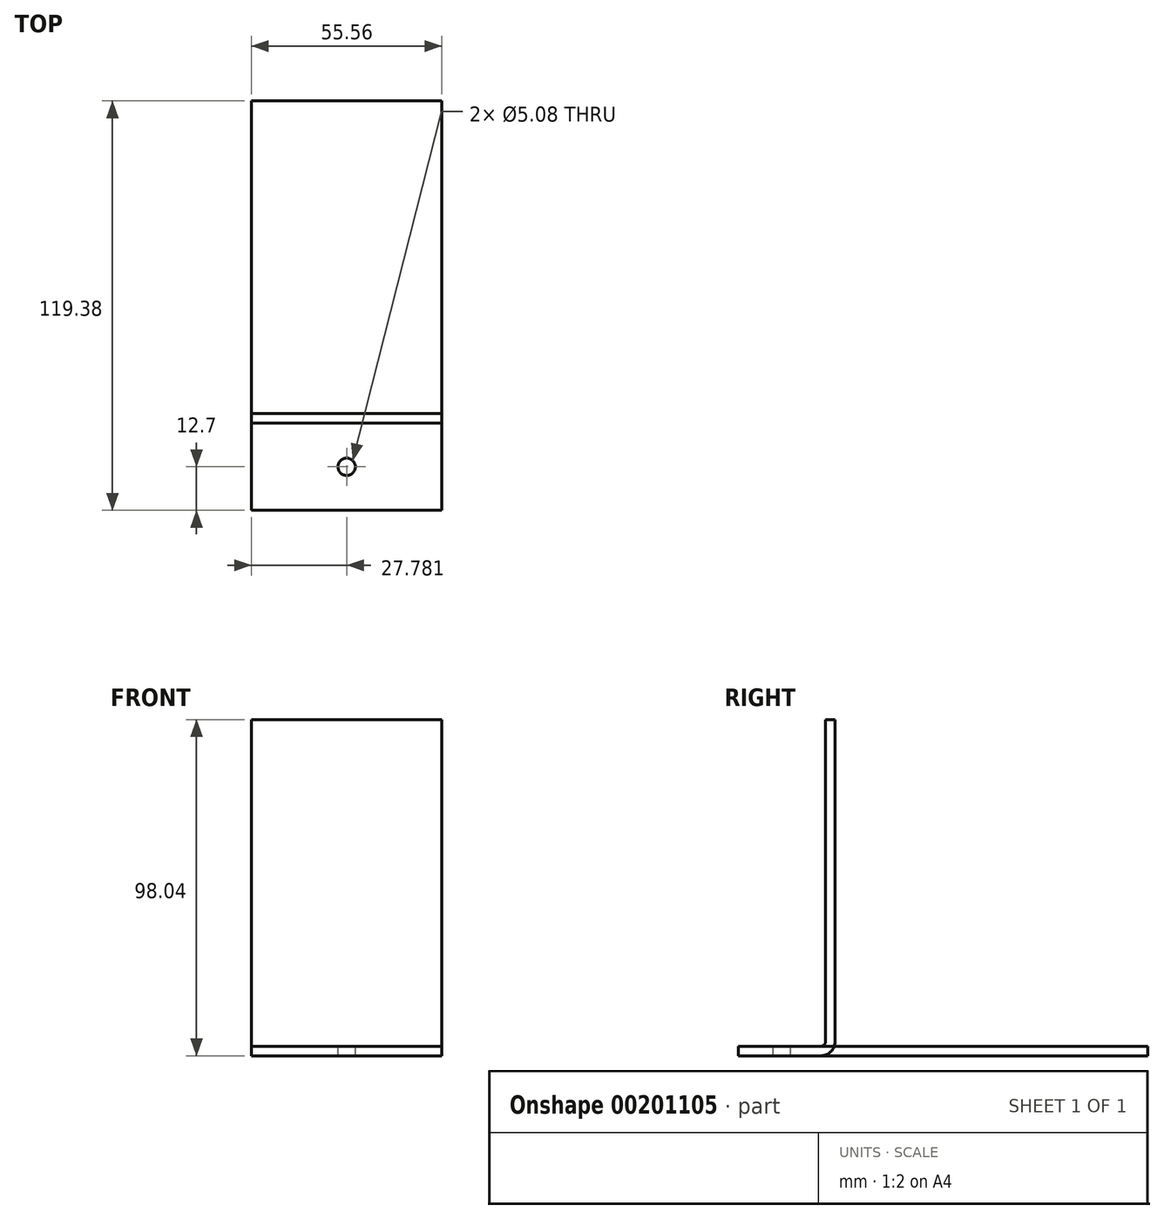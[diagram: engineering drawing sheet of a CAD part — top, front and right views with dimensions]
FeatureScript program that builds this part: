
annotation { "Feature Type Name" : "Feature", "Feature Type Description" : "" }
export const myFeature = defineFeature(function(context is Context, id is Id, definition is map)
    precondition{}
    {
        {
            var Q0;
            Q0=qCreatedBy(makeId("Right.planeOp"),FACE);
            var sketch = newSketch(context, id + "F0", { "sketchPlane" : qUnion([Q0])});
            skLineSegment(sketch, "E0", {"start": v(0, 0) * mm, "end": v(24.13, 0) * mm});
            skLineSegment(sketch, "E1", {"start": v(25.4, 1.27) * mm, "end": v(25.4, 95.25) * mm});
            skPoint(sketch, "E2.visualSharp", {"position": v(25.4, 0) * mm});
            skArc(sketch, "E2.filletArc", {"start": v(24.13, 0) * mm, "mid": v(25.03, 0.37) * mm, "end": v(25.4, 1.27) * mm});
            skLineSegment(sketch, "E3.0", {"start": v(28.2, 1.27) * mm, "end": v(28.2, 95.25) * mm});
            skArc(sketch, "E3.1", {"start": v(24.13, -2.8) * mm, "mid": v(27, -1.6) * mm, "end": v(28.2, 1.27) * mm});
            skLineSegment(sketch, "E3.2", {"start": v(0, -2.8) * mm, "end": v(24.13, -2.8) * mm});
            skLineSegment(sketch, "E4", {"start": v(28.2, 95.25) * mm, "end": v(25.4, 95.25) * mm});
            skLineSegment(sketch, "E5", {"start": v(0, -2.8) * mm, "end": v(0, 0) * mm});
            skSolve(sketch);
        }
        {
            var Q0;
            Q0=qSketchRegion(id+"F0",true);
            extrude(context, id + "F1", {"entities" : qUnion([Q0]), "depth" : 55.56 * mm});
        }
        {
            var Q0;
            Q0=makeQuery(id+"F1.opExtrude","SWEPT_FACE",FACE,{"disambiguationData":[OSD([sQuery(id+"F0.wireOp",EDGE,"E0")])]});
            var sketch = newSketch(context, id + "F2", { "sketchPlane" : qUnion([Q0])});
            skCircle(sketch, "E6", {"center": v(27.78, 12.7) * mm, "radius": 2.54 * mm});
            skLineSegment(sketch, "E7", {"start": v(0, 0) * mm, "end": v(27.78, 12.7) * mm, "construction": true});
            skLineSegment(sketch, "E8", {"start": v(55.56, 0) * mm, "end": v(27.78, 12.7) * mm, "construction": true});
            skLineSegment(sketch, "E9", {"start": v(27.78, 12.7) * mm, "end": v(27.78, 0) * mm, "construction": true});
            skLineSegment(sketch, "E10", {"start": v(27.78, 12.7) * mm, "end": v(27.78, 25.4) * mm, "construction": true});
            skPoint(sketch, "E10.endSnap0", {"position": v(27.78, 24.13) * mm});
            skSolve(sketch);
        }
        {
            var Q0;
            Q0=qSketchRegion(id+"F2",true);
            extrude(context, id + "F3", {"entities" : qUnion([Q0]), "operationType" : NewBodyOperationType.REMOVE, "oppositeDirection" : true, "depth" : 25.4 * mm});
        }
        {
            var Q0;
            Q0=makeQuery(id+"F1.opExtrude","SWEPT_FACE",FACE,{"disambiguationData":[OSD([sQuery(id+"F0.wireOp",EDGE,"E5")])]});
            extrude(context, id + "F4", {"entities" : qUnion([Q0]), "oppositeDirection" : true, "depth" : 119.38 * mm});
        }
        {
            var Q0;
            Q0=makeQuery(id+"F4.opExtrude","SWEPT_FACE",FACE,{"disambiguationData":[OSD([sQuery(id+"F0.wireOp",EDGE,"E0"),sQuery(id+"F0.wireOp",EDGE,"E5")])]});
            var sketch = newSketch(context, id + "F5", { "sketchPlane" : qUnion([Q0])});
            skCircle(sketch, "E11.0", {"center": v(27.78, 12.7) * mm, "radius": 2.54 * mm});
            skSolve(sketch);
        }
        {
            var Q0;
            Q0=qSketchRegion(id+"F5",true);
            extrude(context, id + "F6", {"entities" : qUnion([Q0]), "operationType" : NewBodyOperationType.REMOVE, "oppositeDirection" : true, "depth" : 25.4 * mm});
        }
    });
